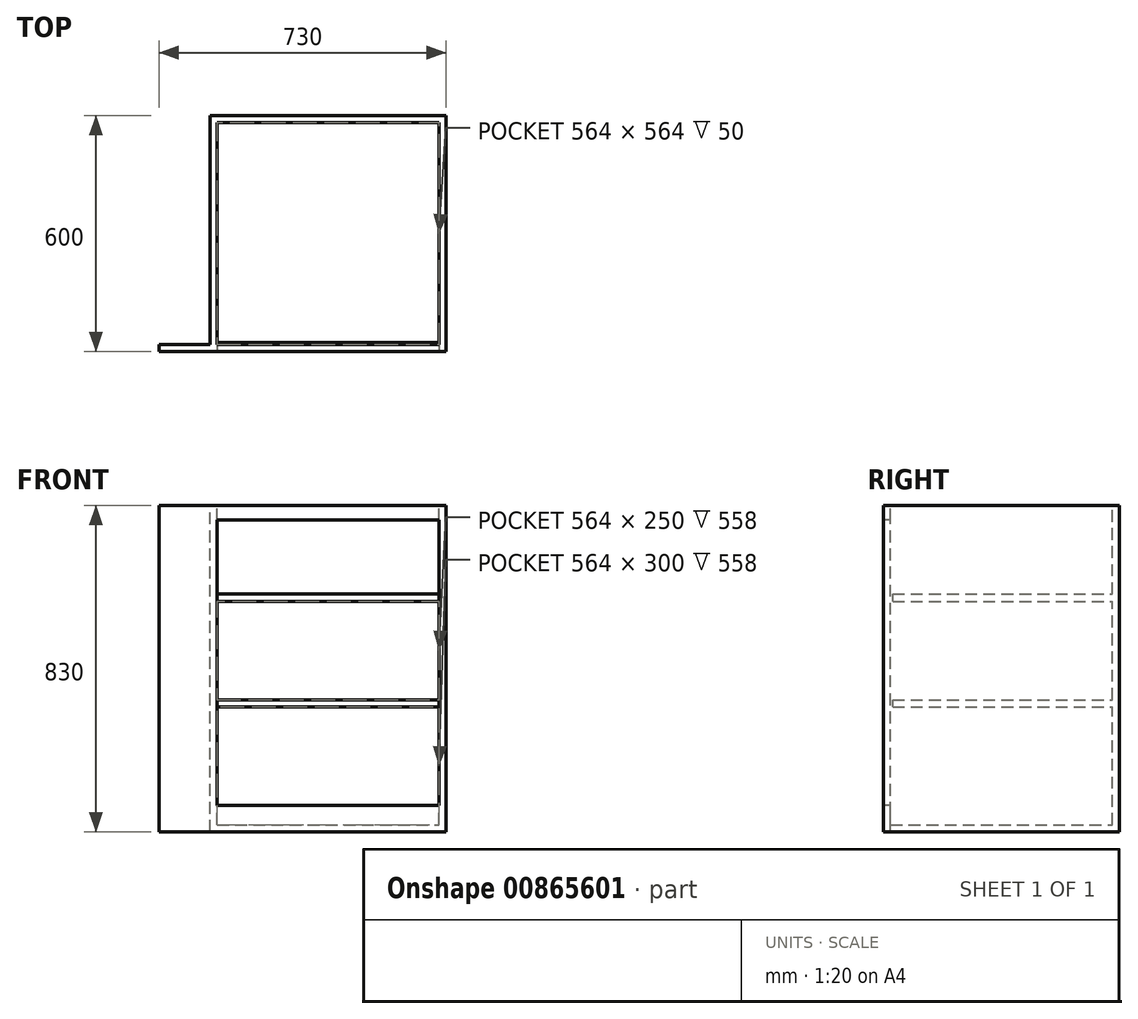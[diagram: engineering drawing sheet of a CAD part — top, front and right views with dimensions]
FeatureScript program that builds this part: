
annotation { "Feature Type Name" : "Feature", "Feature Type Description" : "" }
export const myFeature = defineFeature(function(context is Context, id is Id, definition is map)
    precondition{}
    {
        {
            var Q0;
            Q0=qCreatedBy(makeId("Top.planeOp"),FACE);
            var sketch = newSketch(context, id + "F0", { "sketchPlane" : qUnion([Q0])});
            skLineSegment(sketch, "E0.bottom", {"start": v(0, 0) * mm, "end": v(600, 0) * mm});
            skLineSegment(sketch, "E0.top", {"start": v(0, 600) * mm, "end": v(600, 600) * mm});
            skLineSegment(sketch, "E0.left", {"start": v(0, 18) * mm, "end": v(0, 600) * mm});
            skLineSegment(sketch, "E0.right", {"start": v(600, 0) * mm, "end": v(600, 600) * mm});
            skLineSegment(sketch, "E1.0", {"start": v(18, 582) * mm, "end": v(582, 582) * mm});
            skLineSegment(sketch, "E1.1", {"start": v(18, 18) * mm, "end": v(18, 582) * mm});
            skLineSegment(sketch, "E1.2", {"start": v(18, 18) * mm, "end": v(582, 18) * mm});
            skLineSegment(sketch, "E1.3", {"start": v(582, 18) * mm, "end": v(582, 582) * mm});
            skLineSegment(sketch, "E2.bottom", {"start": v(0, 0) * mm, "end": v(-130, 0) * mm});
            skLineSegment(sketch, "E2.top", {"start": v(0, 18) * mm, "end": v(-130, 18) * mm});
            skLineSegment(sketch, "E2.right", {"start": v(-130, 0) * mm, "end": v(-130, 18) * mm});
            skSolve(sketch);
        }
        {
            var Q0;
            Q0 = qSketchRegion(id + "F0", true);
            extrude(context, id + "F1", {"entities" : qUnion([Q0]), "oppositeDirection" : true, "depth" : 830 * mm, "offsetDistance" : 25 * mm});
        }
        {
            var Q0;
            Q0=makeQuery(id+"F1.opExtrude","SWEPT_FACE",FACE,{"disambiguationData":[OSD([sQuery(id+"F0.wireOp",EDGE,"E0.bottom"),sQuery(id+"F0.wireOp",EDGE,"E2.bottom")])]});
            var sketch = newSketch(context, id + "F2", { "sketchPlane" : qUnion([Q0])});
            skLineSegment(sketch, "E3.right", {"start": v(600, 0) * mm, "end": v(600, -830) * mm});
            skLineSegment(sketch, "E4.top", {"start": v(300, -830) * mm, "end": v(600, -830) * mm});
            skLineSegment(sketch, "E4.left", {"start": v(300, -38) * mm, "end": v(300, -762) * mm});
            skLineSegment(sketch, "E5", {"start": v(18, -762) * mm, "end": v(582, -762) * mm});
            skLineSegment(sketch, "E6", {"start": v(18, -38) * mm, "end": v(582, -38) * mm});
            skLineSegment(sketch, "E7", {"start": v(582, -38) * mm, "end": v(582, -762) * mm});
            skLineSegment(sketch, "E8", {"start": v(18, -38) * mm, "end": v(18, -762) * mm});
            skPoint(sketch, "E9.orphan", {"position": v(0, 0) * mm});
            skSolve(sketch);
        }
        {
            var Q0;
            {var subQ0=sQuery(id+"F2.wireOp",EDGE,"E4.left");Q0=makeQuery(id+"F2.imprint","IMPRINT",FACE,{"disambiguationData":[TD([[makeQuery(id+"F2.imprint","IMPRINT",EDGE,{"derivedFrom":subQ0}),-1.0]])]});}
            var Q1;
            {var subQ0=sQuery(id+"F2.wireOp",EDGE,"E4.left");Q1=makeQuery(id+"F2.imprint","IMPRINT",FACE,{"disambiguationData":[TD([[makeQuery(id+"F2.imprint","IMPRINT",EDGE,{"derivedFrom":subQ0}),1.0]])]});}
            extrude(context, id + "F3", {"entities" : qUnion([Q0, Q1]), "operationType" : NewBodyOperationType.REMOVE, "oppositeDirection" : true, "depth" : 244 * mm, "offsetDistance" : 25 * mm});
        }
        {
            var Q0;
            Q0=makeQuery(id+"F1.opExtrude","CAP_FACE",FACE,{"disambiguationData":[OSD([sQuery(id+"F0.wireOp",EDGE,"E0.bottom"),sQuery(id+"F0.wireOp",EDGE,"E0.top"),sQuery(id+"F0.wireOp",EDGE,"E0.left"),sQuery(id+"F0.wireOp",EDGE,"E0.right"),sQuery(id+"F0.wireOp",EDGE,"E1.0"),sQuery(id+"F0.wireOp",EDGE,"E1.1"),sQuery(id+"F0.wireOp",EDGE,"E1.2"),sQuery(id+"F0.wireOp",EDGE,"E1.3"),sQuery(id+"F0.wireOp",EDGE,"E2.bottom"),sQuery(id+"F0.wireOp",EDGE,"E2.top"),sQuery(id+"F0.wireOp",EDGE,"E2.right")])],"isStart":false});
            var sketch = newSketch(context, id + "F4", { "sketchPlane" : qUnion([Q0])});
            skLineSegment(sketch, "E10.bottom", {"start": v(18, -18) * mm, "end": v(582, -18) * mm});
            skLineSegment(sketch, "E10.top", {"start": v(18, -582) * mm, "end": v(582, -582) * mm});
            skLineSegment(sketch, "E10.left", {"start": v(18, -18) * mm, "end": v(18, -582) * mm});
            skLineSegment(sketch, "E10.right", {"start": v(582, -18) * mm, "end": v(582, -582) * mm});
            skSolve(sketch);
        }
        {
            var Q0;
            Q0=makeQuery(id+"F4.imprint","IMPRINT",FACE,{"disambiguationData":[TD([[makeQuery(id+"F4.imprint","IMPRINT",EDGE,{"derivedFrom":sQuery(id+"F4.wireOp",EDGE,"E10.bottom")}),-1.0]])]});
            extrude(context, id + "F5", {"entities" : qUnion([Q0]), "operationType" : NewBodyOperationType.ADD, "oppositeDirection" : true, "depth" : 18 * mm, "offsetDistance" : 25 * mm});
        }
        {
            var Q0;
            Q0=makeQuery(id+"F1.opExtrude","SWEPT_FACE",FACE,{"disambiguationData":[OSD([sQuery(id+"F0.wireOp",EDGE,"E1.0")])]});
            var sketch = newSketch(context, id + "F6", { "sketchPlane" : qUnion([Q0])});
            skLineSegment(sketch, "E11.bottom", {"start": v(18, -512) * mm, "end": v(582, -512) * mm});
            skLineSegment(sketch, "E11.top", {"start": v(18, -494) * mm, "end": v(582, -494) * mm});
            skLineSegment(sketch, "E11.left", {"start": v(18, -512) * mm, "end": v(18, -494) * mm});
            skLineSegment(sketch, "E11.right", {"start": v(582, -512) * mm, "end": v(582, -494) * mm});
            skLineSegment(sketch, "E12.bottom", {"start": v(18, -812) * mm, "end": v(582, -812) * mm, "construction": true});
            skLineSegment(sketch, "E12.top", {"start": v(18, 0) * mm, "end": v(582, 0) * mm, "construction": true});
            skLineSegment(sketch, "E12.left", {"start": v(18, -812) * mm, "end": v(18, 0) * mm, "construction": true});
            skLineSegment(sketch, "E12.right", {"start": v(582, -812) * mm, "end": v(582, 0) * mm, "construction": true});
            skLineSegment(sketch, "E13.bottom", {"start": v(18, -244) * mm, "end": v(582, -244) * mm});
            skLineSegment(sketch, "E13.top", {"start": v(18, -226) * mm, "end": v(582, -226) * mm});
            skLineSegment(sketch, "E13.left", {"start": v(18, -244) * mm, "end": v(18, -226) * mm});
            skLineSegment(sketch, "E13.right", {"start": v(582, -244) * mm, "end": v(582, -226) * mm});
            skSolve(sketch);
        }
        {
            var Q0;
            Q0=makeQuery(id+"F6.imprint","IMPRINT",FACE,{"disambiguationData":[TD([[makeQuery(id+"F6.imprint","IMPRINT",EDGE,{"derivedFrom":sQuery(id+"F6.wireOp",EDGE,"E13.bottom")}),1.0]])]});
            var Q1;
            Q1=makeQuery(id+"F6.imprint","IMPRINT",FACE,{"disambiguationData":[TD([[makeQuery(id+"F6.imprint","IMPRINT",EDGE,{"derivedFrom":sQuery(id+"F6.wireOp",EDGE,"E11.bottom")}),1.0]])]});
            extrude(context, id + "F7", {"entities" : qUnion([Q0, Q1]), "operationType" : NewBodyOperationType.ADD, "depth" : 558 * mm, "offsetDistance" : 25 * mm});
        }
    });
